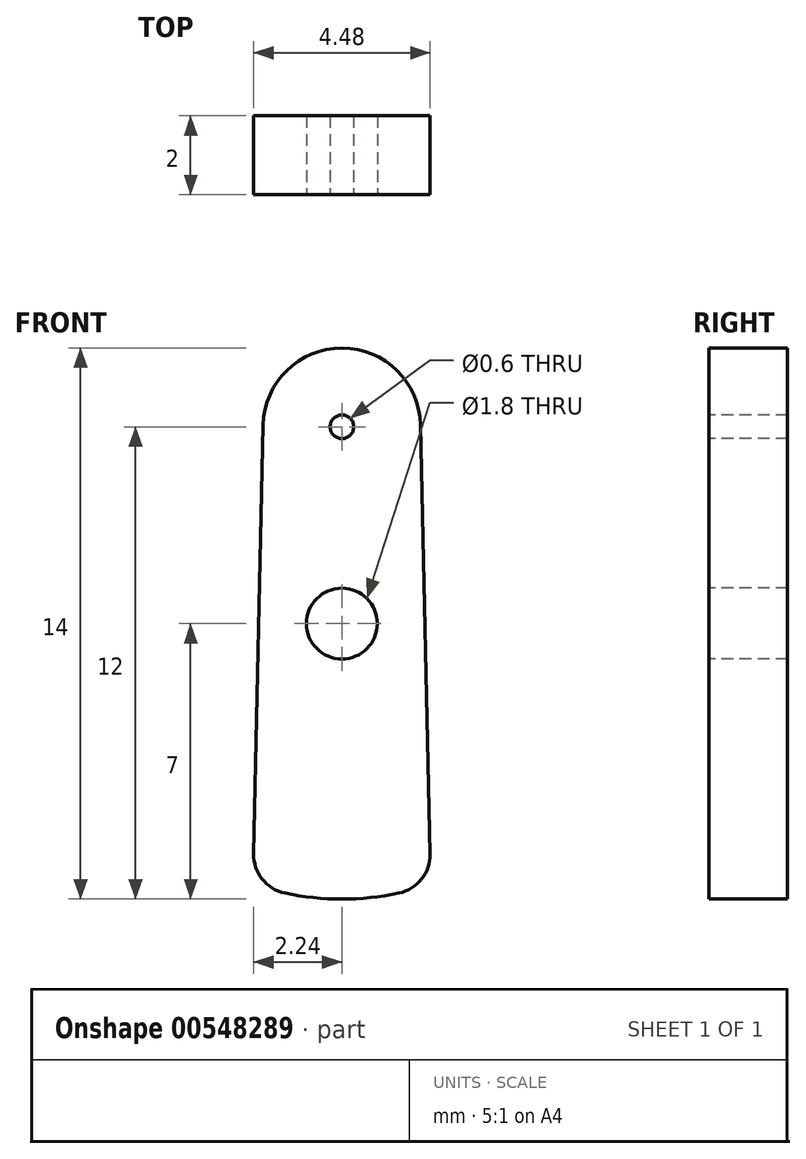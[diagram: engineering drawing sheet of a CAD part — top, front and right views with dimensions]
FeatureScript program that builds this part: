
annotation { "Feature Type Name" : "Feature", "Feature Type Description" : "" }
export const myFeature = defineFeature(function(context is Context, id is Id, definition is map)
    precondition{}
    {
        {
            var Q0;
            Q0=qCreatedBy(makeId("Front.planeOp"),FACE);
            var sketch = newSketch(context, id + "F0", { "sketchPlane" : qUnion([Q0])});
            skArc(sketch, "E0", {"start": v(-1.45, -6.85) * mm, "mid": v(0, -7) * mm, "end": v(1.45, -6.85) * mm});
            skCircle(sketch, "E1", {"center": v(0, 5) * mm, "radius": 2 * mm});
            skLineSegment(sketch, "E2", {"start": v(-2, 5.04) * mm, "end": v(-2.24, -5.85) * mm});
            skLineSegment(sketch, "E3", {"start": v(2, 5.04) * mm, "end": v(2.24, -5.85) * mm});
            skPoint(sketch, "E4.visualSharp", {"position": v(-2.26, -6.63) * mm});
            skArc(sketch, "E4.filletArc", {"start": v(-2.24, -5.85) * mm, "mid": v(-2.02, -6.5) * mm, "end": v(-1.45, -6.85) * mm});
            skPoint(sketch, "E5.visualSharp", {"position": v(2.26, -6.63) * mm});
            skArc(sketch, "E5.filletArc", {"start": v(1.45, -6.85) * mm, "mid": v(2.02, -6.5) * mm, "end": v(2.24, -5.85) * mm});
            skSolve(sketch);
        }
        {
            var Q0;
            {var subQ0=sQuery(id+"F0.wireOp",EDGE,"E1");var subQ1=makeQuery(id+"F0.imprint","INTERSECT",VERTEX,{"derivedFrom":[subQ0,sQuery(id+"F0.wireOp",EDGE,"E2")]});Q0=makeQuery(id+"F0.imprint","IMPRINT",FACE,{"disambiguationData":[TD([[makeQuery(id+"F0.imprint","IMPRINT",EDGE,{"disambiguationData":[TD([[subQ1,1.0]])],"derivedFrom":subQ0}),1.0]])]});}
            var Q1;
            Q1=makeQuery(id+"F0.imprint","IMPRINT",FACE,{"disambiguationData":[TD([[makeQuery(id+"F0.imprint","IMPRINT",EDGE,{"derivedFrom":sQuery(id+"F0.wireOp",EDGE,"E0")}),1.0]])]});
            extrude(context, id + "F1", {"entities" : qUnion([Q0, Q1]), "endBound" : BoundingType.SYMMETRIC, "depth" : 2 * mm, "offsetDistance" : 25 * mm});
        }
        {
            var Q0;
            Q0=makeQuery(id+"F1.opExtrude","CAP_FACE",FACE,{"disambiguationData":[OSD([sQuery(id+"F0.wireOp",EDGE,"E0"),sQuery(id+"F0.wireOp",EDGE,"E1"),sQuery(id+"F0.wireOp",EDGE,"E2"),sQuery(id+"F0.wireOp",EDGE,"E3"),sQuery(id+"F0.wireOp",EDGE,"E4.filletArc"),sQuery(id+"F0.wireOp",EDGE,"E5.filletArc")])],"isStart":false});
            var sketch = newSketch(context, id + "F2", { "sketchPlane" : qUnion([Q0])});
            skCircle(sketch, "E6", {"center": v(0, 0) * mm, "radius": 0.9 * mm});
            skCircle(sketch, "E7", {"center": v(0, 5) * mm, "radius": 0.3 * mm});
            skSolve(sketch);
        }
        {
            var Q0;
            Q0 = qSketchRegion(id + "F2", true);
            extrude(context, id + "F3", {"entities" : qUnion([Q0]), "operationType" : NewBodyOperationType.REMOVE, "endBound" : BoundingType.THROUGH_ALL, "oppositeDirection" : true, "depth" : 25 * mm, "offsetDistance" : 25 * mm});
        }
    });
